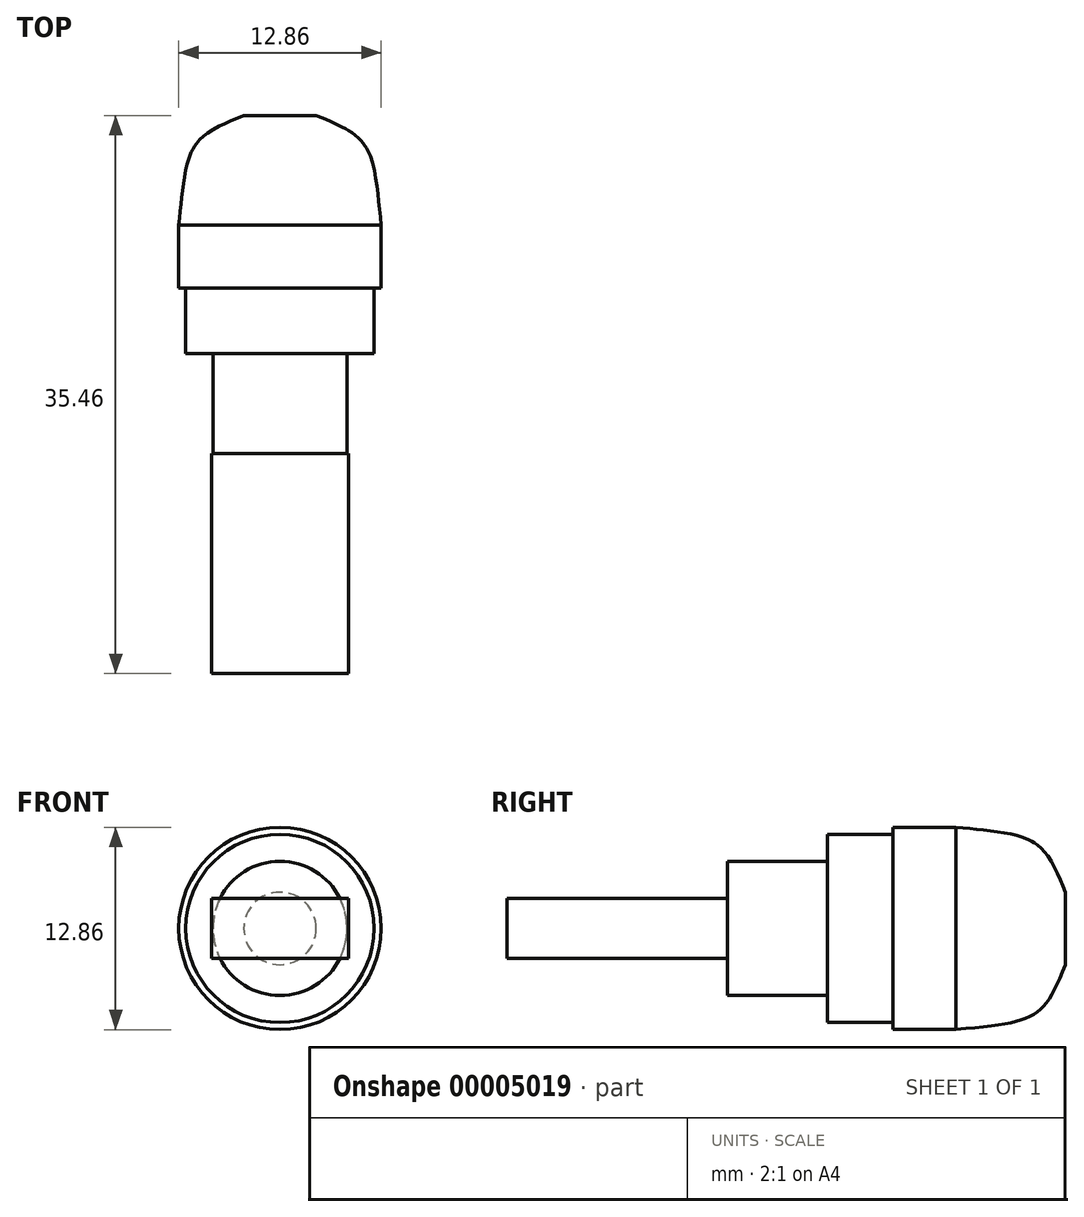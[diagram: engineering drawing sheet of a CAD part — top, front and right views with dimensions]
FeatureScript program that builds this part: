
annotation { "Feature Type Name" : "Feature", "Feature Type Description" : "" }
export const myFeature = defineFeature(function(context is Context, id is Id, definition is map)
    precondition{}
    {
        {
            var Q0;
            Q0=qCreatedBy(makeId("Top.planeOp"),FACE);
            var sketch = newSketch(context, id + "F0", { "sketchPlane" : qUnion([Q0])});
            skLineSegment(sketch, "E0", {"start": v(0, 0) * mm, "end": v(0, 21.46) * mm});
            skLineSegment(sketch, "E1", {"start": v(0, 21.46) * mm, "end": v(2.3, 21.46) * mm});
            skFitSpline(sketch, "E2", {"points": [v(2.3, 21.46) * mm, v(6.42, 14.5) * mm], "startDerivative": vector(10.85, -4.32) * mm, "endDerivative": vector(1.5, -15) * mm});
            skLineSegment(sketch, "E3", {"start": v(6.42, 14.5) * mm, "end": v(6.42, 10.5) * mm});
            skLineSegment(sketch, "E4", {"start": v(6.42, 10.5) * mm, "end": v(5.98, 10.5) * mm});
            skLineSegment(sketch, "E5", {"start": v(5.98, 10.5) * mm, "end": v(5.98, 6.33) * mm});
            skLineSegment(sketch, "E6", {"start": v(5.98, 6.33) * mm, "end": v(4.26, 6.33) * mm});
            skLineSegment(sketch, "E7", {"start": v(4.26, 6.33) * mm, "end": v(4.26, 0) * mm});
            skLineSegment(sketch, "E8", {"start": v(4.26, 0) * mm, "end": v(0, 0) * mm});
            skLineSegment(sketch, "E9", {"start": v(6.43, 14.5) * mm, "end": v(6.43, 19.5) * mm, "construction": true});
            skLineSegment(sketch, "E10", {"start": v(6.42, 19.5) * mm, "end": v(5.93, 19.5) * mm, "construction": true});
            skSolve(sketch);
        }
        {
            var Q0;
            Q0 = qSketchRegion(id + "F0", true);
            var Q1;
            Q1=sQuery(id+"F0.wireOp",EDGE,"E0");
            revolve(context, id + "F1", {"entities" : qUnion([Q0]), "axis" : qUnion([Q1]), "revolveType" : RevolveType.FULL});
        }
        {
            var Q0;
            Q0=makeQuery(id+"F1.opRevolve","SWEPT_FACE",FACE,{"disambiguationData":[OSD([sQuery(id+"F0.wireOp",EDGE,"E8")])]});
            var sketch = newSketch(context, id + "F2", { "sketchPlane" : qUnion([Q0])});
            skLineSegment(sketch, "E11.bottom", {"start": v(-4.35, 1.9) * mm, "end": v(4.35, 1.9) * mm});
            skLineSegment(sketch, "E11.top", {"start": v(-4.35, -1.9) * mm, "end": v(4.35, -1.9) * mm});
            skLineSegment(sketch, "E11.left", {"start": v(-4.35, 1.9) * mm, "end": v(-4.35, -1.9) * mm});
            skLineSegment(sketch, "E11.right", {"start": v(4.35, 1.9) * mm, "end": v(4.35, -1.9) * mm});
            skSolve(sketch);
        }
        {
            var Q0;
            Q0 = qSketchRegion(id + "F2", true);
            extrude(context, id + "F3", {"entities" : qUnion([Q0]), "operationType" : NewBodyOperationType.ADD, "depth" : 14 * mm});
        }
    });
